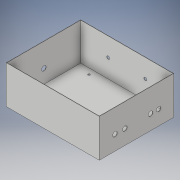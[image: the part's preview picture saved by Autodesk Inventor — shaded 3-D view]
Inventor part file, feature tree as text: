
AUTODESK INVENTOR PART (.ipt)
format: ipt  version: 2018 (Build 220112000, 112)  size: 157,184 bytes
history: native  units: in
note: dims shown in document units (in); Inventor stores cm internally (conversion verified against a paired STEP export)
features: extrude x6, sketch x6
ambient origin geometry x8: Origin, YZ Plane, XZ Plane, XY Plane, X Axis, Y Axis, Z Axis, Center Point
bodies: Solid1 (feature_tree)
feature tree (12):
  extrude  "Extrusion1"  Depth=4.0in
  extrude  "Extrusion2"  Depth=4.96in
  extrude  "Extrusion3"  Depth=2.0in TaperAngle=0.0deg
  extrude  "Extrusion4"  Depth=0.164in
  extrude  "Extrusion5"  Depth=3.937in
  extrude  "Extrusion6"  Depth=0.112in
  sketch  "Sketch1"  dims[d0=5.0in d1=4.0in]
  sketch  "Sketch2"  dims[d2=0.04in d3=0.0in d4=4.96in]
  sketch  "Sketch3"  dims[d5=3.96in d6=2.0in d7=0.0in]
  sketch  "Sketch4"  dims[d10=0.164in d12=0.164in]
  sketch  "Sketch5"  dims[d13=0.0in d14=0.0in d15=3.937in]
  sketch  "Sketch6"  dims[d16=3.937in d23=0.112in d24=0.112in d25=0.112in d26=0.0in d27=0.0in d28=0.25in d29=0.112in d30=0.0in d31=0.0115in d32=0.0in d33=0.781in d34=0.438in d35=0.0in d36=1.375in d37=0.0in d38=0.532in d39=0.0in d40=0.25in d41=0.25in d42=0.25in d43=0.25in d44=0.0in d45=0.0in]
